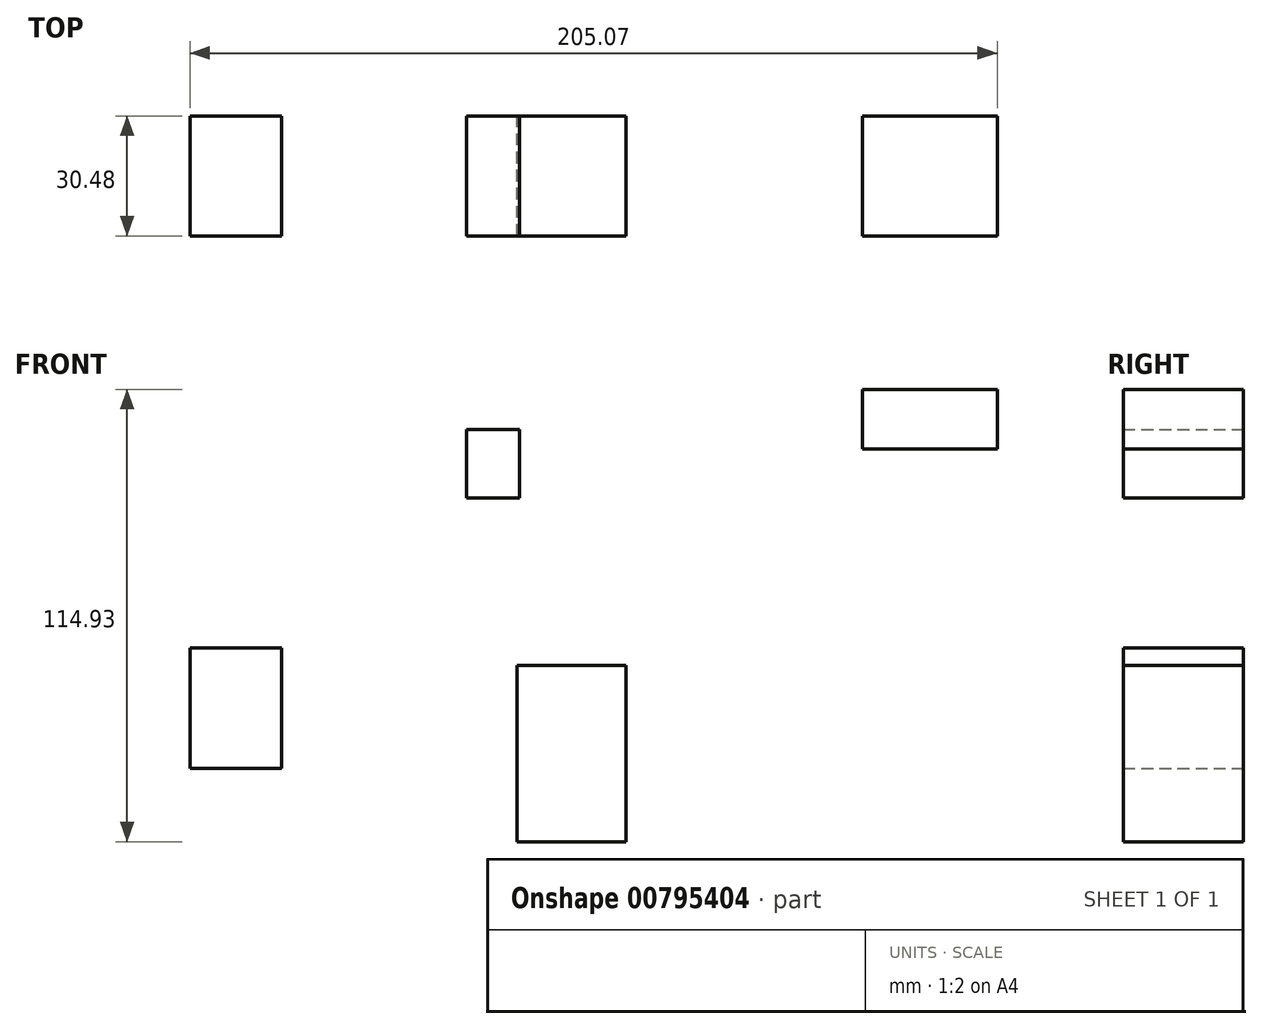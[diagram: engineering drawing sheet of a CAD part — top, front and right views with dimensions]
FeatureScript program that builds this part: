
annotation { "Feature Type Name" : "Feature", "Feature Type Description" : "" }
export const myFeature = defineFeature(function(context is Context, id is Id, definition is map)
    precondition{}
    {
        {
            var Q0;
            Q0=qCreatedBy(makeId("Front.planeOp"),FACE);
            var sketch = newSketch(context, id + "F0", { "sketchPlane" : qUnion([Q0])});
            skLineSegment(sketch, "E0.bottom", {"start": v(-104.87, 63.25) * mm, "end": v(-91.43, 63.25) * mm});
            skLineSegment(sketch, "E0.top", {"start": v(-104.87, 45.92) * mm, "end": v(-91.43, 45.92) * mm});
            skLineSegment(sketch, "E0.left", {"start": v(-104.87, 63.25) * mm, "end": v(-104.87, 45.92) * mm});
            skLineSegment(sketch, "E0.right", {"start": v(-91.43, 63.25) * mm, "end": v(-91.43, 45.92) * mm});
            skLineSegment(sketch, "E1.bottom", {"start": v(-175.08, 7.78) * mm, "end": v(-151.8, 7.78) * mm});
            skLineSegment(sketch, "E1.top", {"start": v(-175.08, -22.82) * mm, "end": v(-151.8, -22.82) * mm});
            skLineSegment(sketch, "E1.left", {"start": v(-175.08, 7.78) * mm, "end": v(-175.08, -22.82) * mm});
            skLineSegment(sketch, "E1.right", {"start": v(-151.8, 7.78) * mm, "end": v(-151.8, -22.82) * mm});
            skLineSegment(sketch, "E2.bottom", {"start": v(-92.1, 3.37) * mm, "end": v(-64.33, 3.37) * mm});
            skLineSegment(sketch, "E2.top", {"start": v(-92.1, -41.45) * mm, "end": v(-64.33, -41.45) * mm});
            skLineSegment(sketch, "E2.left", {"start": v(-92.1, 3.37) * mm, "end": v(-92.1, -41.45) * mm});
            skLineSegment(sketch, "E2.right", {"start": v(-64.33, 3.37) * mm, "end": v(-64.33, -41.45) * mm});
            skLineSegment(sketch, "E3.bottom", {"start": v(-4.34, 73.48) * mm, "end": v(30, 73.48) * mm});
            skLineSegment(sketch, "E3.top", {"start": v(-4.34, 58.32) * mm, "end": v(30, 58.32) * mm});
            skLineSegment(sketch, "E3.left", {"start": v(-4.34, 73.48) * mm, "end": v(-4.34, 58.32) * mm});
            skLineSegment(sketch, "E3.right", {"start": v(30, 73.48) * mm, "end": v(30, 58.32) * mm});
            skSolve(sketch);
        }
        {
            var Q0;
            Q0 = qSketchRegion(id + "F0", true);
            var Q1;
            Q1=sQuery(id+"F0.wireOp",EDGE,"E0.top");
            var Q2;
            Q2=sQuery(id+"F0.wireOp",EDGE,"E0.left");
            var Q3;
            Q3=sQuery(id+"F0.wireOp",EDGE,"E0.right");
            var Q4;
            Q4=sQuery(id+"F0.wireOp",EDGE,"E1.bottom");
            var Q5;
            Q5=sQuery(id+"F0.wireOp",EDGE,"E1.top");
            var Q6;
            Q6=sQuery(id+"F0.wireOp",EDGE,"E1.left");
            var Q7;
            Q7=sQuery(id+"F0.wireOp",EDGE,"E1.right");
            var Q8;
            Q8=sQuery(id+"F0.wireOp",EDGE,"E2.bottom");
            var Q9;
            Q9=sQuery(id+"F0.wireOp",EDGE,"E2.top");
            var Q10;
            Q10=sQuery(id+"F0.wireOp",EDGE,"E2.left");
            var Q11;
            Q11=sQuery(id+"F0.wireOp",EDGE,"E2.right");
            var Q12;
            Q12=sQuery(id+"F0.wireOp",EDGE,"E3.bottom");
            var Q13;
            Q13=sQuery(id+"F0.wireOp",EDGE,"E3.top");
            var Q14;
            Q14=sQuery(id+"F0.wireOp",EDGE,"E3.left");
            var Q15;
            Q15=sQuery(id+"F0.wireOp",EDGE,"E3.right");
            var Q16;
            Q16=sQuery(id+"F0.wireOp",EDGE,"E0.bottom");
            extrude(context, id + "F1", {"entities" : qUnion([Q0]), "surfaceEntities" : qUnion([Q1, Q2, Q3, Q4, Q5, Q6, Q7, Q8, Q9, Q10, Q11, Q12, Q13, Q14, Q15, Q16]), "depth" : 30.48 * mm, "offsetDistance" : 30.48 * mm});
        }
    });
